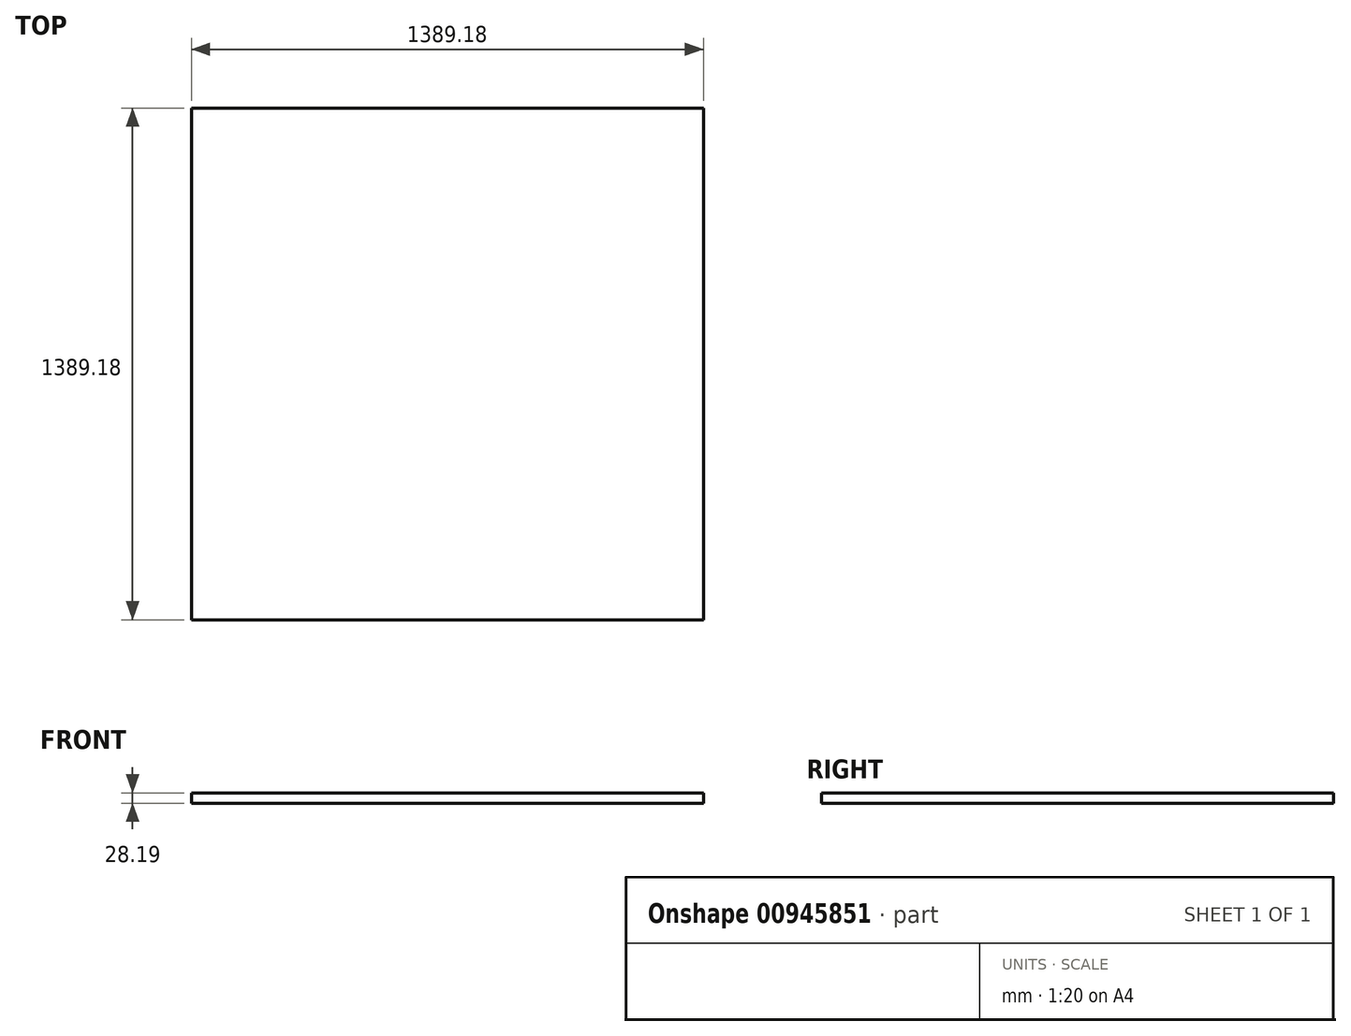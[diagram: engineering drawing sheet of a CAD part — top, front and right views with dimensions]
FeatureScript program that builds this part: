
annotation { "Feature Type Name" : "Feature", "Feature Type Description" : "" }
export const myFeature = defineFeature(function(context is Context, id is Id, definition is map)
    precondition{}
    {
        {
            var Q0;
            Q0=qCreatedBy(makeId("Top.planeOp"),FACE);
            var sketch = newSketch(context, id + "F0", { "sketchPlane" : qUnion([Q0])});
            skLineSegment(sketch, "E0.bottom", {"start": v(-1389.18, 1389.18) * mm, "end": v(0, 1389.18) * mm});
            skLineSegment(sketch, "E0.top", {"start": v(-1389.18, 0) * mm, "end": v(0, 0) * mm});
            skLineSegment(sketch, "E0.left", {"start": v(-1389.18, 1389.18) * mm, "end": v(-1389.18, 0) * mm});
            skLineSegment(sketch, "E0.right", {"start": v(0, 1389.18) * mm, "end": v(0, 0) * mm});
            skSolve(sketch);
        }
        {
            var Q0;
            Q0=makeQuery(id+"F0.imprint","IMPRINT",FACE,{"disambiguationData":[TD([[makeQuery(id+"F0.imprint","IMPRINT",EDGE,{"derivedFrom":sQuery(id+"F0.wireOp",EDGE,"E0.bottom")}),-1.0]])]});
            extrude(context, id + "F1", {"entities" : qUnion([Q0]), "depth" : 28.2 * mm, "offsetDistance" : 25.4 * mm});
        }
    });
